# Revit family: Z-C1616D
name_source: partatom
category: Plumbing Fixtures
revit_build: Autodesk Revit 2018 (Build: 20170223_1515(x64)
units: mm (PartAtom-declared; Revit-internal decimal feet)

## family parameters
Cut with Voids When Loaded = Yes
Host = Face
OmniClass Number = 23.65.35.11.14
OmniClass Title = Instantaneous Water Heaters
Part Type = Normal
Room Calculation Point = No
Round Connector Dimension = Use Diameter
Shared = Yes

## types (19) — shared parameters
ADA Compliant = Yes
AKL-Allen Key Latch = No
Assembly Code = D2020200
Body Material = Plastic-Chronomite-Celcon
CL-Cylinder Lock (one per door = No
CW Connection = No
Chassis And Door Material = Metal-Chronomite-Steel_Galvannealed
Cold Water Connection Diameter = 3/4"
Cold Water Connection Radius = 3/8"
Country = U.S.A.
Default Elevation = 0"
Description = Wall Sleeve for Chronomite Laboratories
Flow Activation = 0.20 GPM (0.75 LPM)
HW Connection = No
Height = 6 1/4"
Hot Water Connection Diameter = 3/4"
Hot Water Connection Radius = 3/8"
Housing Depth = 5 1/4"
Housing Description = Vandal resistant rugged cast aluminum housing
Housing Side = 17 5/8"
IAPMO Compliance = ASSE 1069, CSA B125.3-12 and ASSE 1070 compliancy
Installation Type = Wall Mounted
Length = 12 7/8"
Manufacturer = Chronomite
Maximum Ambient Operating Temperature = 104°/110°F
Maximum Operating Pressure = 80PSI
Maximum Pressure = 150 PSI
Maximum Water Temperature = 104°/110°F
Minimum Flow Rate = 0 GPM
Minimum Operating Pressure = 25 PSI
Model = Z-C1616D
Price = Prices may vary. Please consult Manufacturer Representative for most up-to-date price list.
Product Documentation Link = https://www.chronomite.com
Product Page URL = https://www.chronomite.com
SS-Stainless Steel Construction  m(Type 304 No. 4 Satin Finish = No
Shipping Weight = 5 lbs.
URL = www.chronomite.com
Vent Connection = No
Waste Connection = No
Width = 2 3/4"
zero-valued in all types: CWFU, HWFU, WFU

## per-type parameters (varying)
| type | 90°C Wire | Electric Potential | Electrical Current | Power | Temperature Rise @ 0.35 GPM | Temperature Rise @ 0.5 GPM | Temperature Rise @ 1 GPM | Temperature Rise @ 1.5 GPM | Temperature Rise @ 2 GPM |
| CMI-12L/120 | 14 AWG | 120 V | 12 A | 1440 W | 28 °F | 20 °F | 0 °F | 0 °F | 0 °F |
| CMI-12L/208 | 14 AWG | 208 V | 12 A | 2500 W | 49 °F | 34 °F | 0 °F | 0 °F | 0 °F |
| CMI-12L/240 | 14 AWG | 240 V | 12 A | 2880 W | 56 °F | 39 °F | 20 °F | 0 °F | 0 °F |
| CMI-12L/277 | 14 AWG | 277 V | 12 A | 3320 W | 65 °F | 45 °F | 23 °F | 0 °F | 0 °F |
| CMI-15L/120 | 14 AWG | 120 V | 15 A | 1800 W | 35 °F | 25 °F | 0 °F | 0 °F | 0 °F |
| CMI-15L/208 | 14 AWG | 208 V | 15 A | 3120 W | 35 °F | 61 °F | 43 °F | 21 °F | 0 °F |
| CMI-15L/240 | 14 AWG | 240 V | 15 A | 3600 W | 35 °F | 70 °F | 49 °F | 25 °F | 0 °F |
| CMI-15L/277 | 14 AWG | 277 V | 15 A | 4150 W | 70 °F | 57 °F | 28 °F | 0 °F | 0 °F |
| CMI-20L/120 | 12 AWG | 120 V | 20 A | 2400 W | 47 °F | 33 °F | 0 °F | 0 °F | 0 °F |
| CMI-20L/208 | 12 AWG | 208 V | 20 A | 4160 W | 70 °F | 57 °F | 28 °F | 0 °F | 0 °F |
| CMI-20L/240 | 12 AWG | 240 V | 20 A | 4800 W | 70 °F | 66 °F | 33 °F | 22 °F | 0 °F |
| CMI-20L/277 | 12 AWG | 277 V | 20 A | 5540 W | 70 °F | 70 °F | 38 °F | 25 °F | 0 °F |
| CMI-30L/120 | 10 AWG | 120 V | 30 A | 3600 W | 70 °F | 49 °F | 25 °F | 16 °F | 0 °F |
| CMI-30L/208 | 10 AWG | 208 V | 30 A | 6240 W | 70 °F | 70 °F | 43 °F | 28 °F | 21 °F |
| CMI-30L/240 | 10 AWG | 240 V | 30 A | 7200 W | 70 °F | 70 °F | 49 °F | 33 °F | 25 °F |
| CMI-30L/277 | 10 AWG | 277 V | 30 A | 8310 W | 70 °F | 70 °F | 57 °F | 38 °F | 28 °F |
| CMI-40L/208 | 8 AWG | 208 V | 40 A | 8320 W | 70 °F | 70 °F | 57 °F | 38 °F | 28 °F |
| CMI-40L/240 | 8 AWG | 240 V | 40 A | 9600 W | 70 °F | 70 °F | 66 °F | 44 °F | 33 °F |
| CMI-40L/277 | 8 AWG | 277 V | 40 A | 11080 W | 70 °F | 70 °F | 70 °F | 50 °F | 38 °F |

## geometry (parser evidence)
native form markers: Sweep x5
no freeform markers — native parametric forms only
